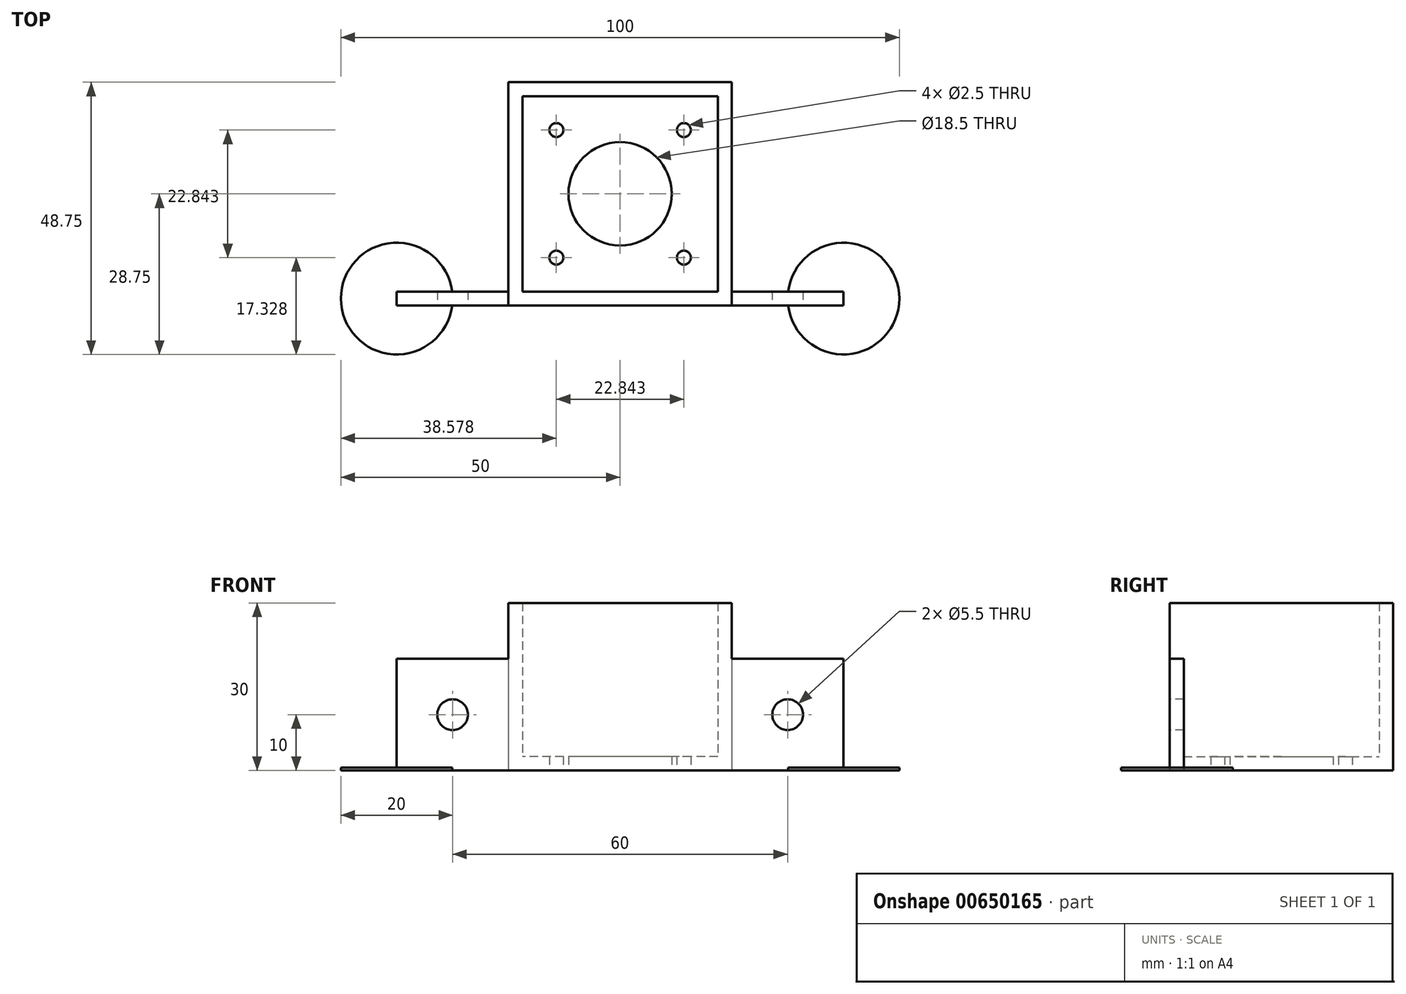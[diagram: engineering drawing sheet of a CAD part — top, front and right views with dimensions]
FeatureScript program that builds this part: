
annotation { "Feature Type Name" : "Feature", "Feature Type Description" : "" }
export const myFeature = defineFeature(function(context is Context, id is Id, definition is map)
    precondition{}
    {
        {
            var Q0;
            Q0=qCreatedBy(makeId("Top.planeOp"),FACE);
            var sketch = newSketch(context, id + "F0", { "sketchPlane" : qUnion([Q0])});
            skLineSegment(sketch, "E0.bottom", {"start": v(20, -20) * mm, "end": v(-20, -20) * mm});
            skLineSegment(sketch, "E0.top", {"start": v(20, 20) * mm, "end": v(-20, 20) * mm});
            skLineSegment(sketch, "E0.left", {"start": v(20, -20) * mm, "end": v(20, 20) * mm});
            skLineSegment(sketch, "E0.right", {"start": v(-20, -20) * mm, "end": v(-20, 20) * mm});
            skPoint(sketch, "E0.middle", {"position": v(0, 0) * mm});
            skSolve(sketch);
        }
        {
            var Q0;
            Q0=makeQuery(id+"F0.imprint","IMPRINT",FACE,{"disambiguationData":[TD([[makeQuery(id+"F0.imprint","IMPRINT",EDGE,{"derivedFrom":sQuery(id+"F0.wireOp",EDGE,"E0.bottom")}),-1.0]])]});
            extrude(context, id + "F1", {"entities" : qUnion([Q0]), "depth" : 30 * mm, "offsetDistance" : 25 * mm});
        }
        {
            var Q0;
            Q0=makeQuery(id+"F1.opExtrude","CAP_FACE",FACE,{"disambiguationData":[OSD([sQuery(id+"F0.wireOp",EDGE,"E0.bottom"),sQuery(id+"F0.wireOp",EDGE,"E0.top"),sQuery(id+"F0.wireOp",EDGE,"E0.left"),sQuery(id+"F0.wireOp",EDGE,"E0.right")])],"isStart":false});
            var Q1;
            Q1=makeQuery(id+"F1.opExtrude","SWEPT_BODY",BODY,{"disambiguationData":[OSD([sQuery(id+"F0.wireOp",EDGE,"E0.bottom"),sQuery(id+"F0.wireOp",EDGE,"E0.top"),sQuery(id+"F0.wireOp",EDGE,"E0.left"),sQuery(id+"F0.wireOp",EDGE,"E0.right")])]});
            shell(context, id + "F2", {"entities" : qUnion([Q0]), "parts" : qUnion([Q1]), "thickness" : 2.5 * mm});
        }
        {
            var Q0;
            Q0=makeQuery(id+"F1.opExtrude","CAP_FACE",FACE,{"disambiguationData":[OSD([sQuery(id+"F0.wireOp",EDGE,"E0.bottom"),sQuery(id+"F0.wireOp",EDGE,"E0.top"),sQuery(id+"F0.wireOp",EDGE,"E0.left"),sQuery(id+"F0.wireOp",EDGE,"E0.right")])],"isStart":true});
            var sketch = newSketch(context, id + "F3", { "sketchPlane" : qUnion([Q0])});
            skLineSegment(sketch, "E1", {"start": v(-20, 20) * mm, "end": v(20, -20) * mm});
            skLineSegment(sketch, "E2.bottom", {"start": v(14.25, -14.25) * mm, "end": v(-14.25, -14.25) * mm});
            skLineSegment(sketch, "E2.top", {"start": v(14.25, 14.25) * mm, "end": v(-14.25, 14.25) * mm});
            skLineSegment(sketch, "E2.left", {"start": v(14.25, -14.25) * mm, "end": v(14.25, 14.25) * mm});
            skLineSegment(sketch, "E2.right", {"start": v(-14.25, -14.25) * mm, "end": v(-14.25, 14.25) * mm});
            skPoint(sketch, "E2.middle", {"position": v(0, 0) * mm});
            skLineSegment(sketch, "E3", {"start": v(-14.25, 14.25) * mm, "end": v(-11.42, 11.42) * mm});
            skLineSegment(sketch, "E4", {"start": v(14.25, 14.25) * mm, "end": v(-14.25, -14.25) * mm});
            skLineSegment(sketch, "E5", {"start": v(14.25, 14.25) * mm, "end": v(11.42, 11.42) * mm});
            skLineSegment(sketch, "E6", {"start": v(-14.25, -14.25) * mm, "end": v(-11.42, -11.42) * mm});
            skLineSegment(sketch, "E7", {"start": v(14.25, -14.25) * mm, "end": v(11.42, -11.42) * mm});
            skSolve(sketch);
        }
        {
            var Q0;
            Q0=sQuery(id+"F3.wireOp",VERTEX,"E3.end");
            var Q1;
            Q1=sQuery(id+"F3.wireOp",VERTEX,"E5.end");
            var Q2;
            Q2=sQuery(id+"F3.wireOp",VERTEX,"E6.end");
            var Q3;
            Q3=sQuery(id+"F3.wireOp",VERTEX,"E7.end");
            var Q4;
            Q4=makeQuery(id+"F1.opExtrude","SWEPT_BODY",BODY,{"disambiguationData":[OSD([sQuery(id+"F0.wireOp",EDGE,"E0.bottom"),sQuery(id+"F0.wireOp",EDGE,"E0.top"),sQuery(id+"F0.wireOp",EDGE,"E0.left"),sQuery(id+"F0.wireOp",EDGE,"E0.right")])]});
            hole(context, id + "F4", {"style" : HoleStyle.SIMPLE, "endStyle" : HoleEndStyle.THROUGH, "standardTappedOrClearance" : lookupTablePath({ "standard" : "ISO", "engagement" : "75%", "pitch" : "0.5 mm", "size" : "M3", "type" : "Tapped" }), "standardBlindInLast" : lookupTablePath({ "standard" : "ISO", "fit" : "Normal", "engagement" : "75%", "pitch" : "0.5 mm", "size" : "M3", "type" : "Clearance & tapped" }), "holeDiameter" : 2.5 * mm, "majorDiameter" : 3 * mm, "showTappedDepth" : true, "isTappedThrough" : true, "tappedDepth" : 12 * mm, "tapClearance" : 3, "locations" : qUnion([Q0, Q1, Q2, Q3]), "scope" : qUnion([Q4])});
        }
        {
            var Q0;
            Q0=sQuery(id+"F3.wireOp",VERTEX,"E2.middle");
            var Q1;
            Q1=makeQuery(id+"F1.opExtrude","SWEPT_BODY",BODY,{"disambiguationData":[OSD([sQuery(id+"F0.wireOp",EDGE,"E0.bottom"),sQuery(id+"F0.wireOp",EDGE,"E0.top"),sQuery(id+"F0.wireOp",EDGE,"E0.left"),sQuery(id+"F0.wireOp",EDGE,"E0.right")])]});
            hole(context, id + "F5", {"style" : HoleStyle.SIMPLE, "endStyle" : HoleEndStyle.THROUGH, "standardTappedOrClearance" : lookupTablePath({ "standard" : "ISO", "engagement" : "75%", "pitch" : "1.5 mm", "size" : "M20", "type" : "Tapped" }), "standardBlindInLast" : lookupTablePath({ "standard" : "ISO", "fit" : "Normal", "engagement" : "75%", "pitch" : "1.5 mm", "size" : "M20", "type" : "Clearance & tapped" }), "holeDiameter" : 18.5 * mm, "majorDiameter" : 20 * mm, "showTappedDepth" : true, "isTappedThrough" : true, "tappedDepth" : 12 * mm, "tapClearance" : 3, "locations" : qUnion([Q0]), "scope" : qUnion([Q1])});
        }
        {
            var Q0;
            Q0=makeQuery(id+"F1.opExtrude","SWEPT_FACE",FACE,{"disambiguationData":[OSD([sQuery(id+"F0.wireOp",EDGE,"E0.bottom")])]});
            var sketch = newSketch(context, id + "F6", { "sketchPlane" : qUnion([Q0])});
            skLineSegment(sketch, "E8", {"start": v(-20, 20) * mm, "end": v(-20, 0) * mm});
            skLineSegment(sketch, "E9", {"start": v(-20, 0) * mm, "end": v(-40, 0) * mm});
            skLineSegment(sketch, "E10", {"start": v(-40, 0) * mm, "end": v(-40, 20) * mm});
            skLineSegment(sketch, "E11", {"start": v(-40, 20) * mm, "end": v(-20, 20) * mm});
            skLineSegment(sketch, "E12", {"start": v(20, 0) * mm, "end": v(20, 20) * mm});
            skLineSegment(sketch, "E13", {"start": v(20, 20) * mm, "end": v(40, 20) * mm});
            skLineSegment(sketch, "E14", {"start": v(40, 20) * mm, "end": v(40, 0) * mm});
            skLineSegment(sketch, "E15", {"start": v(40, 0) * mm, "end": v(20, 0) * mm});
            skSolve(sketch);
        }
        {
            var Q0;
            Q0=makeQuery(id+"F6.imprint","IMPRINT",FACE,{"disambiguationData":[TD([[makeQuery(id+"F6.imprint","IMPRINT",EDGE,{"derivedFrom":sQuery(id+"F6.wireOp",EDGE,"E8")}),-1.0]])]});
            var Q1;
            Q1=makeQuery(id+"F6.imprint","IMPRINT",FACE,{"disambiguationData":[TD([[makeQuery(id+"F6.imprint","IMPRINT",EDGE,{"derivedFrom":sQuery(id+"F6.wireOp",EDGE,"E12")}),1.0]])]});
            extrude(context, id + "F7", {"entities" : qUnion([Q0, Q1]), "operationType" : NewBodyOperationType.ADD, "oppositeDirection" : true, "depth" : 2.5 * mm, "offsetDistance" : 25 * mm});
        }
        {
            var Q0;
            {var subQ0=sQuery(id+"F0.wireOp",EDGE,"E0.bottom");Q0=makeQuery(id+"F7.boolean.opBoolean","MERGE",FACE,{"derivedFrom":[makeQuery(id+"F1.opExtrude","SWEPT_FACE",FACE,{"disambiguationData":[OSD([subQ0])]}),makeQuery(id+"F7.opExtrude","CAP_FACE",FACE,{"disambiguationData":[OSD([subQ0,sQuery(id+"F0.wireOp",EDGE,"E0.left"),sQuery(id+"F6.wireOp",EDGE,"YcH1IbRK-Fubo-6M4A-jsZJ-0cTAbH08h2BH"),sQuery(id+"F6.wireOp",EDGE,"czgiRdVX-cyB2-a0rB-xg3X-hIJvz8wkPDxN"),sQuery(id+"F6.wireOp",EDGE,"sOMLhsTz-RUlp-jlYm-Dmgp-thhRutMS3HEr"),sQuery(id+"F6.wireOp",EDGE,"Lgr9pfcB-t7hp-tKtm-aT1I-7EVMpjSboAUS")])],"isStart":true}),makeQuery(id+"F7.opExtrude","CAP_FACE",FACE,{"disambiguationData":[OSD([sQuery(id+"F6.wireOp",EDGE,"E8"),sQuery(id+"F6.wireOp",EDGE,"E9"),sQuery(id+"F6.wireOp",EDGE,"E10"),sQuery(id+"F6.wireOp",EDGE,"E11")])],"isStart":true})]});}
            var sketch = newSketch(context, id + "F8", { "sketchPlane" : qUnion([Q0])});
            skLineSegment(sketch, "E16", {"start": v(-20, 20) * mm, "end": v(-40, 0) * mm});
            skPoint(sketch, "E17", {"position": v(-30, 10) * mm});
            skLineSegment(sketch, "E18", {"start": v(20, 20) * mm, "end": v(40, 0) * mm});
            skPoint(sketch, "E19", {"position": v(30, 10) * mm});
            skSolve(sketch);
        }
        {
            var Q0;
            Q0=sQuery(id+"F8.wireOp",VERTEX,"E17");
            var Q1;
            Q1=sQuery(id+"F8.wireOp",VERTEX,"E19");
            var Q2;
            Q2=makeQuery(id+"F1.opExtrude","SWEPT_BODY",BODY,{"disambiguationData":[OSD([sQuery(id+"F0.wireOp",EDGE,"E0.bottom"),sQuery(id+"F0.wireOp",EDGE,"E0.top"),sQuery(id+"F0.wireOp",EDGE,"E0.left"),sQuery(id+"F0.wireOp",EDGE,"E0.right")])]});
            hole(context, id + "F9", {"style" : HoleStyle.SIMPLE, "endStyle" : HoleEndStyle.THROUGH, "standardTappedOrClearance" : lookupTablePath({ "fit" : "Normal", "standard" : "ISO", "size" : "M5", "type" : "Clearance" }), "standardBlindInLast" : lookupTablePath({ "fit" : "Normal", "standard" : "ISO", "engagement" : "75%", "pitch" : "0.8 mm", "size" : "M5", "type" : "Clearance & tapped" }), "holeDiameter" : 5.5 * mm, "majorDiameter" : 5 * mm, "isTappedThrough" : true, "tappedDepth" : 12 * mm, "tapClearance" : 3, "locations" : qUnion([Q0, Q1]), "scope" : qUnion([Q2])});
        }
        {
            var Q0;
            Q0=makeQuery(id+"F7.boolean.opBoolean","MERGE",FACE,{"derivedFrom":[makeQuery(id+"F1.opExtrude","CAP_FACE",FACE,{"disambiguationData":[OSD([sQuery(id+"F0.wireOp",EDGE,"E0.bottom"),sQuery(id+"F0.wireOp",EDGE,"E0.top"),sQuery(id+"F0.wireOp",EDGE,"E0.left"),sQuery(id+"F0.wireOp",EDGE,"E0.right")])],"isStart":true}),makeQuery(id+"F7.opExtrude","SWEPT_FACE",FACE,{"disambiguationData":[OSD([sQuery(id+"F6.wireOp",EDGE,"E9")])]}),makeQuery(id+"F7.opExtrude","SWEPT_FACE",FACE,{"disambiguationData":[OSD([sQuery(id+"F6.wireOp",EDGE,"E15")])]})]});
            var sketch = newSketch(context, id + "F10", { "sketchPlane" : qUnion([Q0])});
            skPoint(sketch, "E20", {"position": v(-40, 18.75) * mm});
            skCircle(sketch, "E21", {"center": v(-40, 18.75) * mm, "radius": 10 * mm});
            skPoint(sketch, "E22", {"position": v(40, 18.75) * mm});
            skCircle(sketch, "E23", {"center": v(40, 18.75) * mm, "radius": 10 * mm});
            skSolve(sketch);
        }
        {
            var Q0;
            {var subQ1=sQuery(id+"F6.wireOp",EDGE,"E15");var subQ6=makeQuery(id+"F7.opExtrude","SWEPT_EDGE",EDGE,{"disambiguationData":[OSD([sQuery(id+"F6.wireOp",EDGE,"E14"),subQ1])]});Q0=makeQuery(id+"F10.imprint","IMPRINT",FACE,{"disambiguationData":[TD([[makeQuery(id+"F10.imprint","IMPRINT",EDGE,{"derivedFrom":subQ6}),-1.0]])]});}
            var Q1;
            {var subQ1=sQuery(id+"F6.wireOp",EDGE,"E9");var subQ6=makeQuery(id+"F7.opExtrude","SWEPT_EDGE",EDGE,{"disambiguationData":[OSD([subQ1,sQuery(id+"F6.wireOp",EDGE,"E10")])]});Q1=makeQuery(id+"F10.imprint","IMPRINT",FACE,{"disambiguationData":[TD([[makeQuery(id+"F10.imprint","IMPRINT",EDGE,{"derivedFrom":subQ6}),1.0]])]});}
            extrude(context, id + "F11", {"entities" : qUnion([Q0, Q1]), "operationType" : NewBodyOperationType.ADD, "oppositeDirection" : true, "depth" : .5 * mm, "offsetDistance" : 25 * mm});
        }
    });
